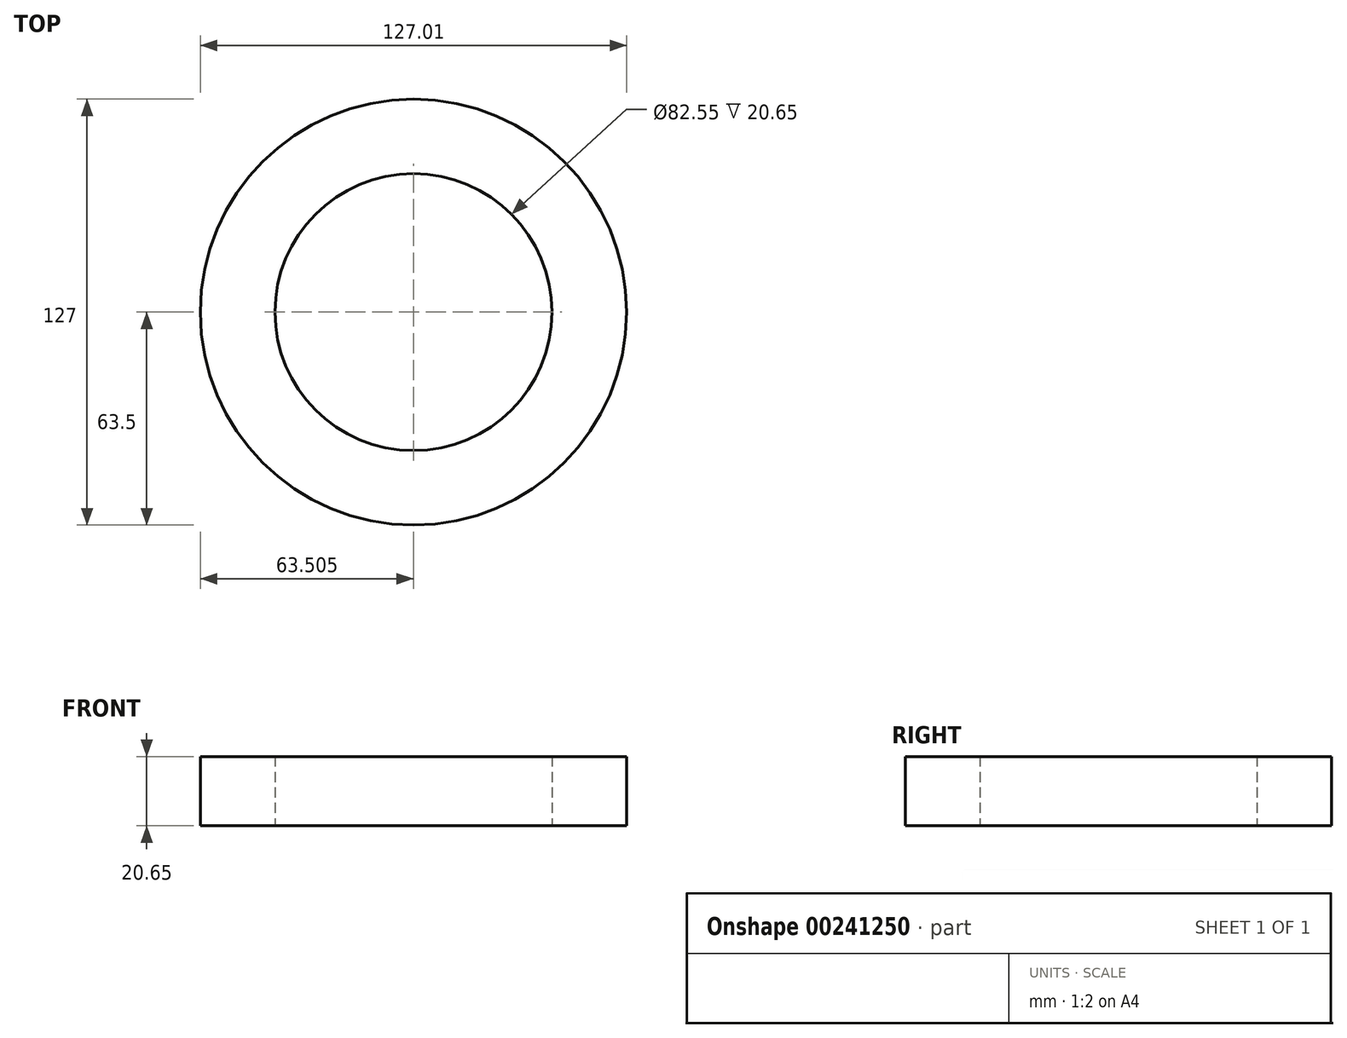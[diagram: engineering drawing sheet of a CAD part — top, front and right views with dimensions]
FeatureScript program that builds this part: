
annotation { "Feature Type Name" : "Feature", "Feature Type Description" : "" }
export const myFeature = defineFeature(function(context is Context, id is Id, definition is map)
    precondition{}
    {
        {
            var Q0;
            Q0=qCreatedBy(makeId("Front.planeOp"),FACE);
            var sketch = newSketch(context, id + "F0", { "sketchPlane" : qUnion([Q0])});
            skLineSegment(sketch, "E0.bottom", {"start": v(0, 0) * mm, "end": v(-3.17, 0) * mm});
            skLineSegment(sketch, "E0.top", {"start": v(0, 20.65) * mm, "end": v(-3.18, 20.65) * mm});
            skLineSegment(sketch, "E0.left", {"start": v(0, 0) * mm, "end": v(0, 20.65) * mm});
            skLineSegment(sketch, "E0.right", {"start": v(-3.17, 0) * mm, "end": v(-3.18, 20.65) * mm});
            skLineSegment(sketch, "E1", {"start": v(44.04, 0) * mm, "end": v(44.04, 38.94) * mm, "construction": true});
            skSolve(sketch);
        }
        {
            var Q0;
            Q0 = qSketchRegion(id + "F0", true);
            var Q1;
            Q1=sQuery(id+"F0.wireOp",EDGE,"E1");
            revolve(context, id + "F1", {"entities" : qUnion([Q0]), "axis" : qUnion([Q1]), "revolveType" : RevolveType.FULL});
        }
        {
            var Q0;
            Q0=qCreatedBy(makeId("Front.planeOp"),FACE);
            var sketch = newSketch(context, id + "F2", { "sketchPlane" : qUnion([Q0])});
            skLineSegment(sketch, "E2.bottom", {"start": v(0, 0) * mm, "end": v(-22.23, 0) * mm});
            skLineSegment(sketch, "E2.top", {"start": v(0, 20.65) * mm, "end": v(-22.23, 20.65) * mm});
            skLineSegment(sketch, "E2.left", {"start": v(0, 0) * mm, "end": v(0, 20.65) * mm});
            skLineSegment(sketch, "E2.right", {"start": v(-22.23, 0) * mm, "end": v(-22.23, 20.65) * mm});
            skLineSegment(sketch, "E3", {"start": v(0, 0) * mm, "end": v(41.28, 0) * mm});
            skLineSegment(sketch, "E4", {"start": v(41.28, 0) * mm, "end": v(41.28, 29.6) * mm, "construction": true});
            skSolve(sketch);
        }
        {
            var Q0;
            Q0 = qSketchRegion(id + "F2", true);
            var Q1;
            Q1=sQuery(id+"F2.wireOp",EDGE,"E4");
            revolve(context, id + "F3", {"operationType" : NewBodyOperationType.ADD, "entities" : qUnion([Q0]), "axis" : qUnion([Q1]), "revolveType" : RevolveType.FULL});
        }
    });
